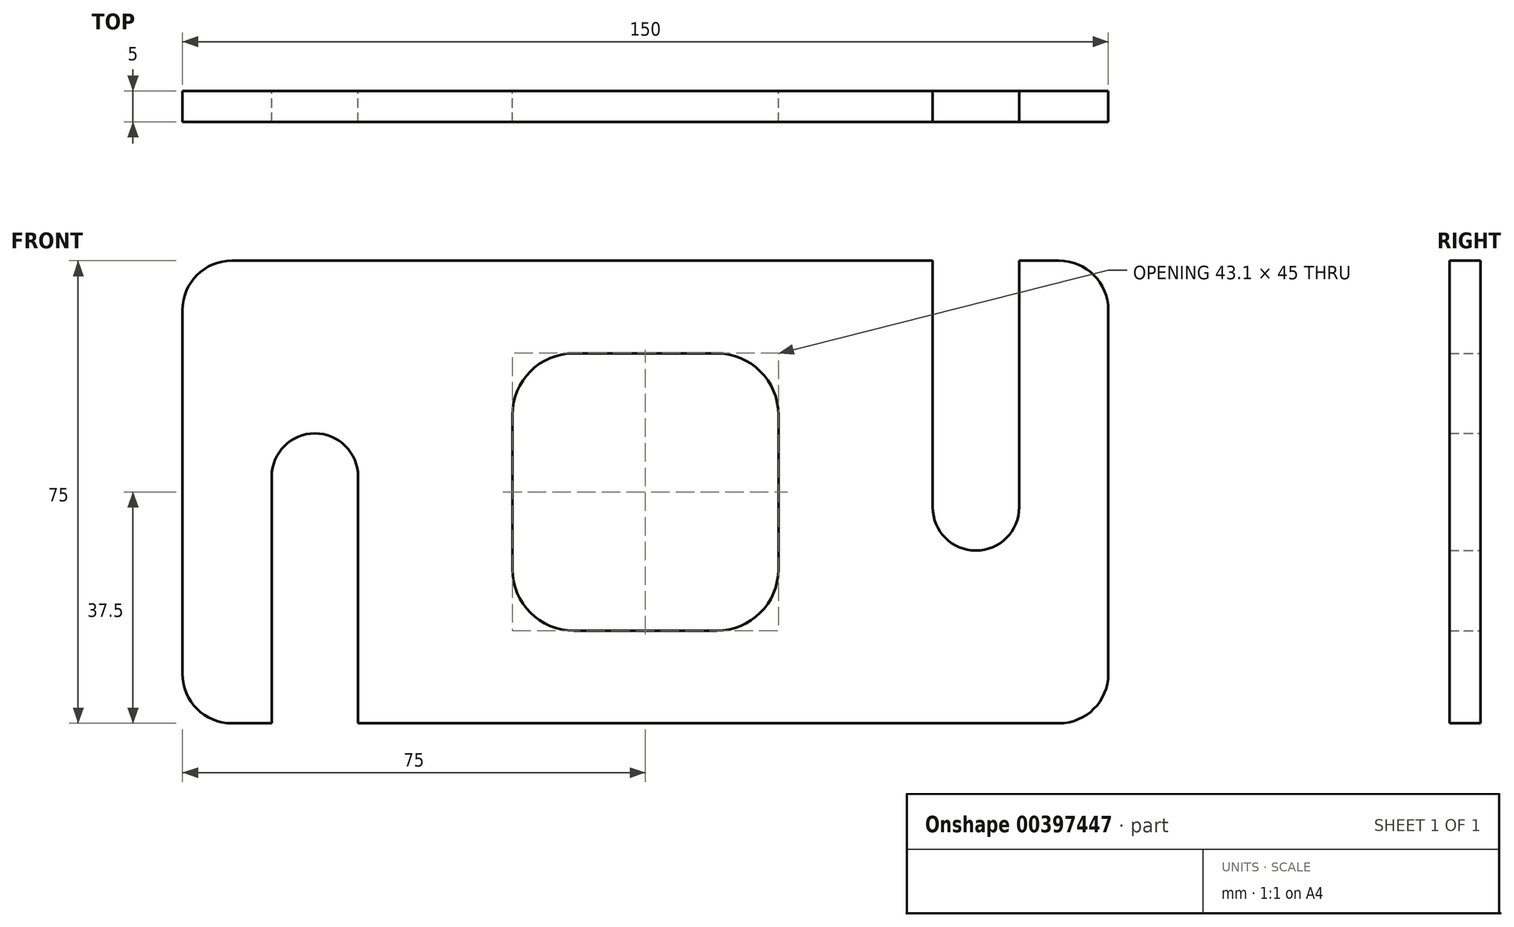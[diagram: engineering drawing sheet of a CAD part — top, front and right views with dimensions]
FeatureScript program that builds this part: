
annotation { "Feature Type Name" : "Feature", "Feature Type Description" : "" }
export const myFeature = defineFeature(function(context is Context, id is Id, definition is map)
    precondition{}
    {
        {
            var Q0;
            Q0=qCreatedBy(makeId("Front.planeOp"),FACE);
            var sketch = newSketch(context, id + "F0", { "sketchPlane" : qUnion([Q0])});
            skLineSegment(sketch, "E0.bottom", {"start": v(-67, -37.5) * mm, "end": v(67, -37.5) * mm});
            skLineSegment(sketch, "E0.top", {"start": v(-67, 37.5) * mm, "end": v(67, 37.5) * mm});
            skLineSegment(sketch, "E0.left", {"start": v(-75, -29.5) * mm, "end": v(-75, 29.5) * mm});
            skLineSegment(sketch, "E0.right", {"start": v(75, -29.5) * mm, "end": v(75, 29.5) * mm});
            skPoint(sketch, "E0.middle", {"position": v(0, 0) * mm});
            skLineSegment(sketch, "E1.bottom", {"start": v(-11.55, 22.5) * mm, "end": v(11.55, 22.5) * mm});
            skLineSegment(sketch, "E1.top", {"start": v(-11.55, -22.5) * mm, "end": v(11.55, -22.5) * mm});
            skLineSegment(sketch, "E1.left", {"start": v(-21.55, 12.5) * mm, "end": v(-21.55, -12.5) * mm});
            skLineSegment(sketch, "E1.right", {"start": v(21.55, 12.5) * mm, "end": v(21.55, -12.5) * mm});
            skPoint(sketch, "E2.visualSharp", {"position": v(-75, 37.5) * mm});
            skArc(sketch, "E2.filletArc", {"start": v(-67, 37.5) * mm, "mid": v(-72.66, 35.16) * mm, "end": v(-75, 29.5) * mm});
            skPoint(sketch, "E3.visualSharp", {"position": v(-75, -37.5) * mm});
            skArc(sketch, "E3.filletArc", {"start": v(-75, -29.5) * mm, "mid": v(-72.66, -35.16) * mm, "end": v(-67, -37.5) * mm});
            skPoint(sketch, "E4.visualSharp", {"position": v(75, -37.5) * mm});
            skArc(sketch, "E4.filletArc", {"start": v(67, -37.5) * mm, "mid": v(72.66, -35.16) * mm, "end": v(75, -29.5) * mm});
            skPoint(sketch, "E5.visualSharp", {"position": v(75, 37.5) * mm});
            skArc(sketch, "E5.filletArc", {"start": v(75, 29.5) * mm, "mid": v(72.66, 35.16) * mm, "end": v(67, 37.5) * mm});
            skPoint(sketch, "E6.visualSharp", {"position": v(-21.55, 22.5) * mm});
            skArc(sketch, "E6.filletArc", {"start": v(-11.55, 22.5) * mm, "mid": v(-18.62, 19.57) * mm, "end": v(-21.55, 12.5) * mm});
            skPoint(sketch, "E7.visualSharp", {"position": v(-21.55, -22.5) * mm});
            skArc(sketch, "E7.filletArc", {"start": v(-21.55, -12.5) * mm, "mid": v(-18.62, -19.57) * mm, "end": v(-11.55, -22.5) * mm});
            skPoint(sketch, "E8.visualSharp", {"position": v(21.55, -22.5) * mm});
            skArc(sketch, "E8.filletArc", {"start": v(11.55, -22.5) * mm, "mid": v(18.62, -19.57) * mm, "end": v(21.55, -12.5) * mm});
            skPoint(sketch, "E9.visualSharp", {"position": v(21.55, 22.5) * mm});
            skArc(sketch, "E9.filletArc", {"start": v(21.55, 12.5) * mm, "mid": v(18.62, 19.57) * mm, "end": v(11.55, 22.5) * mm});
            skLineSegment(sketch, "E10.bottom", {"start": v(-60.55, -37.5) * mm, "end": v(-46.55, -37.5) * mm});
            skLineSegment(sketch, "E10.top", {"start": v(-53.55, 9.5) * mm, "end": v(-53.55, 9.5) * mm});
            skLineSegment(sketch, "E10.left", {"start": v(-60.55, -37.5) * mm, "end": v(-60.55, 2.5) * mm});
            skLineSegment(sketch, "E10.right", {"start": v(-46.55, -37.5) * mm, "end": v(-46.55, 2.5) * mm});
            skPoint(sketch, "E11.visualSharp", {"position": v(-60.55, 9.5) * mm});
            skArc(sketch, "E11.filletArc", {"start": v(-53.55, 9.5) * mm, "mid": v(-58.5, 7.45) * mm, "end": v(-60.55, 2.5) * mm});
            skPoint(sketch, "E12.visualSharp", {"position": v(-46.55, 9.5) * mm});
            skArc(sketch, "E12.filletArc", {"start": v(-46.55, 2.5) * mm, "mid": v(-48.6, 7.45) * mm, "end": v(-53.55, 9.5) * mm});
            skLineSegment(sketch, "E13.bottom", {"start": v(46.55, 37.5) * mm, "end": v(60.55, 37.5) * mm});
            skLineSegment(sketch, "E13.top", {"start": v(53.55, -9.5) * mm, "end": v(53.55, -9.5) * mm});
            skLineSegment(sketch, "E13.left", {"start": v(46.55, 37.5) * mm, "end": v(46.55, -2.5) * mm});
            skLineSegment(sketch, "E13.right", {"start": v(60.55, 37.5) * mm, "end": v(60.55, -2.5) * mm});
            skPoint(sketch, "E14.visualSharp", {"position": v(46.55, -9.5) * mm});
            skArc(sketch, "E14.filletArc", {"start": v(46.55, -2.5) * mm, "mid": v(48.6, -7.45) * mm, "end": v(53.55, -9.5) * mm});
            skPoint(sketch, "E15.visualSharp", {"position": v(60.55, -9.5) * mm});
            skArc(sketch, "E15.filletArc", {"start": v(53.55, -9.5) * mm, "mid": v(58.5, -7.45) * mm, "end": v(60.55, -2.5) * mm});
            skSolve(sketch);
        }
        {
            var Q0;
            Q0=makeQuery(id+"F0.imprint","IMPRINT",FACE,{"disambiguationData":[TD([[makeQuery(id+"F0.imprint","IMPRINT",EDGE,{"derivedFrom":sQuery(id+"F0.wireOp",EDGE,"E0.left")}),-1.0]])]});
            extrude(context, id + "F1", {"entities" : qUnion([Q0]), "depth" : 5 * mm});
        }
    });
